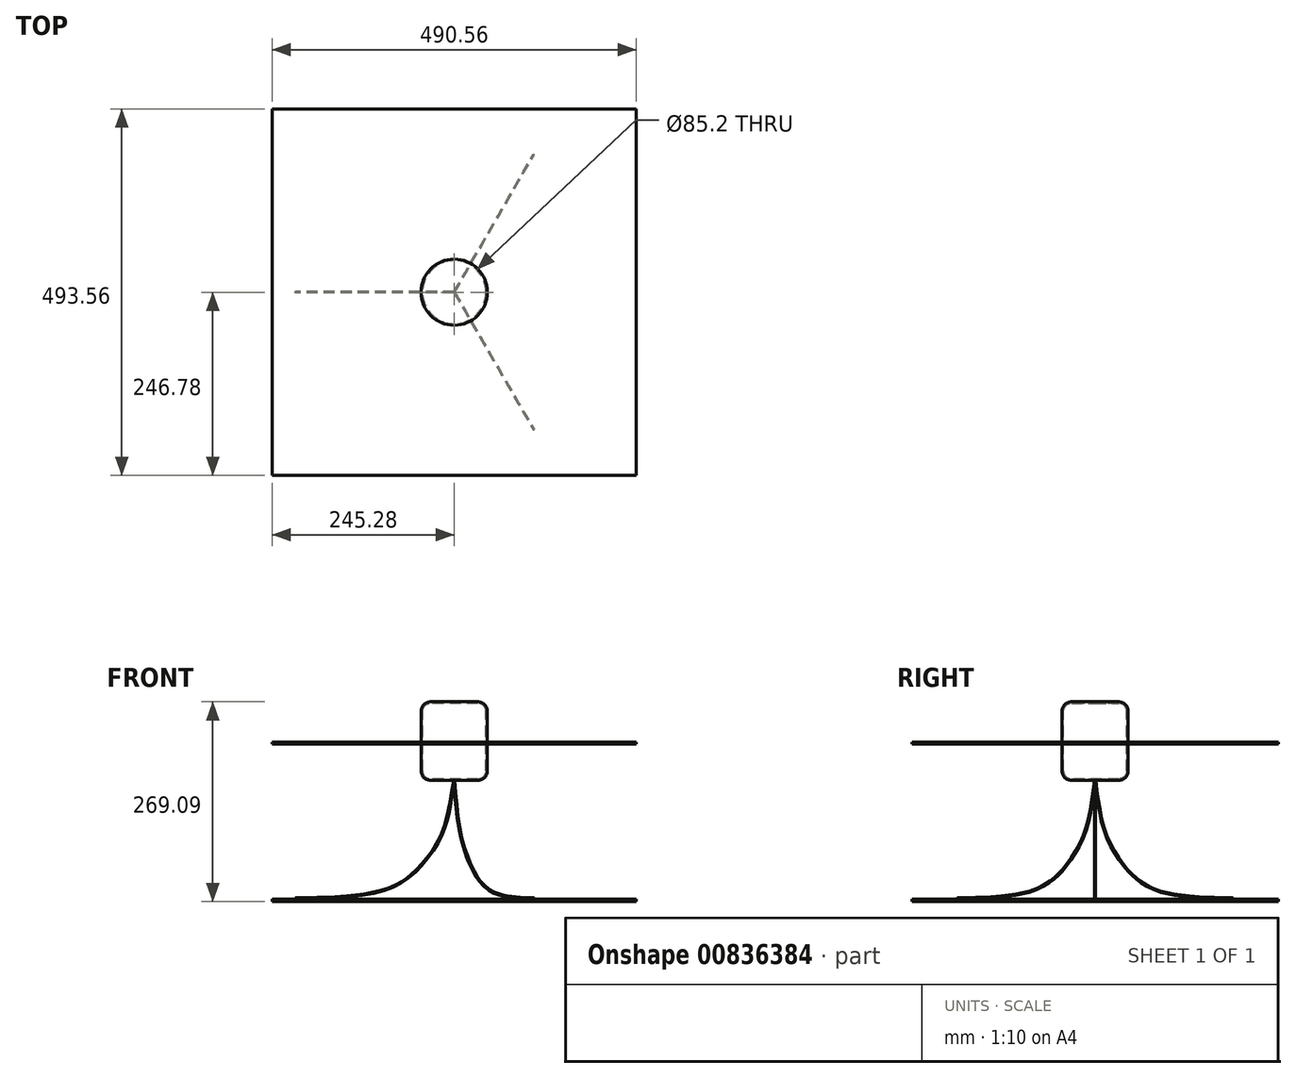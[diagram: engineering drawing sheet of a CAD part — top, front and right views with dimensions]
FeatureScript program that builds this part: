
annotation { "Feature Type Name" : "Feature", "Feature Type Description" : "" }
export const myFeature = defineFeature(function(context is Context, id is Id, definition is map)
    precondition{}
    {
        {
            var Q0;
            Q0=qCreatedBy(makeId("Front.planeOp"),FACE);
            var sketch = newSketch(context, id + "F0", { "sketchPlane" : qUnion([Q0])});
            skLineSegment(sketch, "E0", {"start": v(-44.6, 40.52) * mm, "end": v(-44.6, -40.01) * mm});
            skArc(sketch, "E1", {"start": v(-44.6, -40.01) * mm, "mid": v(-40.92, -48.9) * mm, "end": v(-32.03, -52.58) * mm});
            skArc(sketch, "E2", {"start": v(-32.03, 53.1) * mm, "mid": v(-40.92, 49.41) * mm, "end": v(-44.6, 40.52) * mm});
            skLineSegment(sketch, "E3", {"start": v(-32.03, -52.58) * mm, "end": v(0, -52.58) * mm});
            skLineSegment(sketch, "E4", {"start": v(-32.03, 53.1) * mm, "end": v(0, 53.1) * mm});
            skLineSegment(sketch, "E5.0", {"start": v(-32.03, -50.58) * mm, "end": v(0, -50.58) * mm});
            skLineSegment(sketch, "E5.1", {"start": v(-32.03, 51.1) * mm, "end": v(0, 51.1) * mm});
            skArc(sketch, "E5.2", {"start": v(-32.03, 51.1) * mm, "mid": v(-39.5, 48) * mm, "end": v(-42.6, 40.52) * mm});
            skLineSegment(sketch, "E5.3", {"start": v(-42.6, 40.52) * mm, "end": v(-42.6, -40.01) * mm});
            skArc(sketch, "E5.4", {"start": v(-42.6, -40.01) * mm, "mid": v(-39.5, -47.49) * mm, "end": v(-32.03, -50.58) * mm});
            skLineSegment(sketch, "E6", {"start": v(0, 68.04) * mm, "end": v(0, -61.08) * mm, "construction": true});
            skLineSegment(sketch, "E7", {"start": v(0, 53.1) * mm, "end": v(0, 51.1) * mm});
            skLineSegment(sketch, "E8", {"start": v(0, -50.58) * mm, "end": v(0, -52.58) * mm});
            skSolve(sketch);
        }
        {
            var Q0;
            Q0 = qSketchRegion(id + "F0", true);
            var Q1;
            Q1=sQuery(id+"F0.wireOp",EDGE,"E6");
            revolve(context, id + "F1", {"surfaceOperationType" : NewSurfaceOperationType.NEW, "entities" : qUnion([Q0]), "axis" : qUnion([Q1]), "revolveType" : RevolveType.FULL});
        }
        {
            var Q0;
            Q0=qCreatedBy(makeId("Front.planeOp"),FACE);
            var sketch = newSketch(context, id + "F2", { "sketchPlane" : qUnion([Q0])});
            skFitSpline(sketch, "E9", {"points": [v(0, -52.23) * mm, v(-6.43, -89.56) * mm, v(-17.54, -127.01) * mm, v(-50.29, -173.24) * mm, v(-100.36, -202.13) * mm, v(-214, -211.76) * mm], "startDerivative": vector(-38, -234.02) * mm, "endDerivative": vector(-449.65, -7.84) * mm});
            skSolve(sketch);
        }
        {
            var Q0;
            Q0=qCreatedBy(makeId("Right.planeOp"),FACE);
            cPlane(context, id + "F3", {"entities" : qUnion([Q0]), "cplaneType" : CPlaneType.OFFSET, "offset" : 214 * mm, "oppositeDirection" : true, "width" : 150 * mm, "height" : 150 * mm});
        }
        {
            var Q0;
            Q0=qCreatedBy(id+"F3.planeOp",FACE);
            var sketch = newSketch(context, id + "F4", { "sketchPlane" : qUnion([Q0])});
            skPoint(sketch, "E10.0", {"position": v(0, -211.76) * mm});
            skCircle(sketch, "E11", {"center": v(0, -211.76) * mm, "radius": 0.75 * mm});
            skSolve(sketch);
        }
        {
            var Q0;
            Q0=makeQuery(id+"F4.imprint","IMPRINT",FACE,{"disambiguationData":[TD([[makeQuery(id+"F4.imprint","IMPRINT",EDGE,{"derivedFrom":sQuery(id+"F4.wireOp",EDGE,"E11")}),1.0]])]});
            var Q1;
            Q1=sQuery(id+"F2.wireOp",EDGE,"E9");
            sweep(context, id + "F5", {"profiles" : qUnion([Q0]), "path" : qUnion([Q1])});
        }
        {
            var Q0;
            Q0=makeQuery(id+"F5.opSweep","SWEPT_BODY",BODY,{"disambiguationData":[OSD([sQuery(id+"F2.wireOp",EDGE,"E9"),sQuery(id+"F4.wireOp",EDGE,"E11")])]});
            var Q1;
            Q1=sQuery(id+"F0.wireOp",EDGE,"E6");
            circularPattern(context, id + "F6", {"entities" : qUnion([Q0]), "axis" : qUnion([Q1]), "angle" : 360 * degree, "instanceCount" : 3, "equalSpace" : true});
        }
        {
            var Q0;
            Q0=qCreatedBy(makeId("Top.planeOp"),FACE);
            cPlane(context, id + "F7", {"entities" : qUnion([Q0]), "cplaneType" : CPlaneType.OFFSET, "offset" : 213 * mm, "oppositeDirection" : true, "width" : 150 * mm, "height" : 150 * mm});
        }
        {
            var Q0;
            Q0=qCreatedBy(id+"F7.planeOp",FACE);
            var sketch = newSketch(context, id + "F8", { "sketchPlane" : qUnion([Q0])});
            skLineSegment(sketch, "E12.bottom", {"start": v(-245.28, 246.78) * mm, "end": v(245.28, 246.78) * mm});
            skLineSegment(sketch, "E12.top", {"start": v(-245.28, -246.78) * mm, "end": v(245.28, -246.78) * mm});
            skLineSegment(sketch, "E12.left", {"start": v(-245.28, 246.78) * mm, "end": v(-245.28, -246.78) * mm});
            skLineSegment(sketch, "E12.right", {"start": v(245.28, 246.78) * mm, "end": v(245.28, -246.78) * mm});
            skPoint(sketch, "E12.middle", {"position": v(0, 0) * mm});
            skSolve(sketch);
        }
        {
            var Q0;
            Q0 = qSketchRegion(id + "F8", true);
            extrude(context, id + "F9", {"entities" : qUnion([Q0]), "oppositeDirection" : true, "depth" : 3 * mm, "offsetDistance" : 25 * mm});
        }
        {
            var Q0;
            Q0=makeQuery(id+"F9.opExtrude","SWEPT_BODY",BODY,{"disambiguationData":[OSD([sQuery(id+"F8.wireOp",EDGE,"E12.bottom"),sQuery(id+"F8.wireOp",EDGE,"E12.top"),sQuery(id+"F8.wireOp",EDGE,"E12.left"),sQuery(id+"F8.wireOp",EDGE,"E12.right")])]});
            transform(context, id + "F10", {"entities" : qUnion([Q0]), "transformType" : TransformType.TRANSLATION_3D, "dx" : 0 * mm, "dy" : 0 * mm, "dz" : 212 * mm, "makeCopy" : true});
        }
    });
